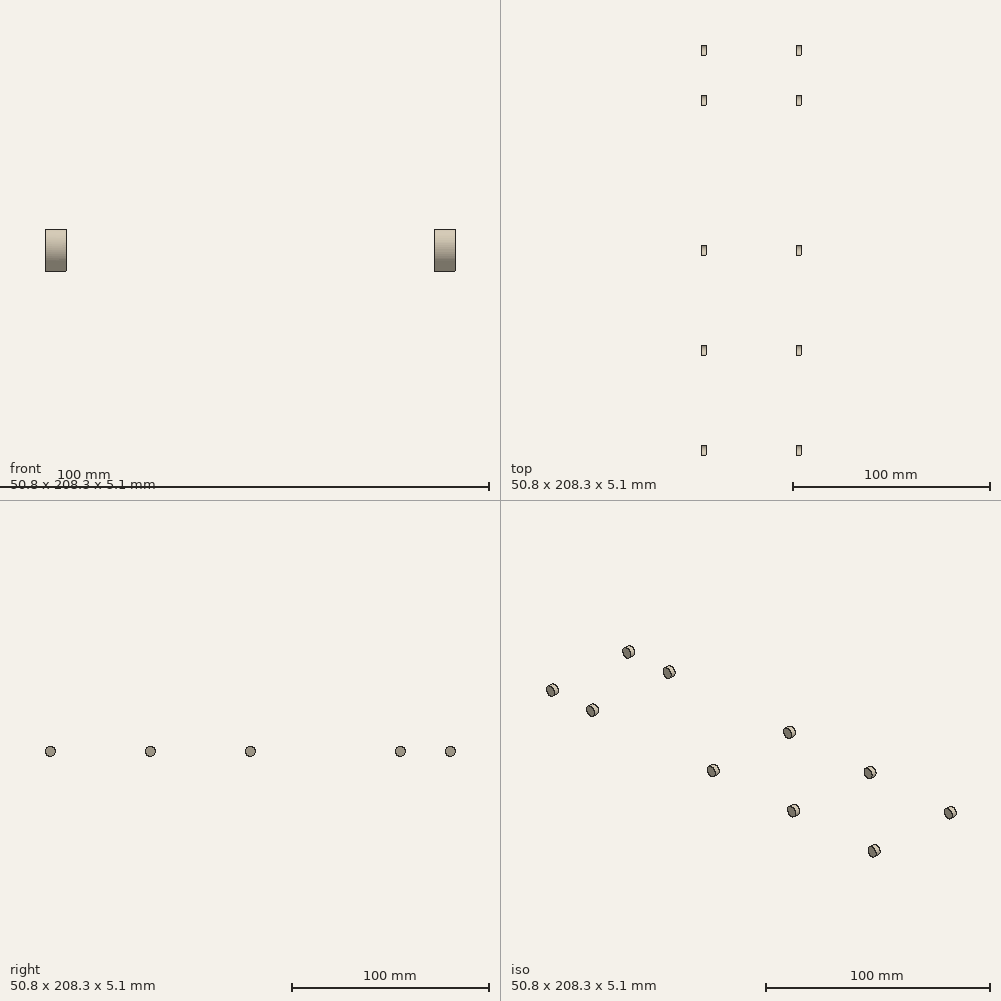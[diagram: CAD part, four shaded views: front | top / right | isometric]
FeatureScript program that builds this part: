
annotation { "Feature Type Name" : "Feature", "Feature Type Description" : "" }
export const myFeature = defineFeature(function(context is Context, id is Id, definition is map)
    precondition{}
    {
        {
            var Q0;
            Q0=qCreatedBy(makeId("Front.planeOp"),FACE);
            var sketch = newSketch(context, id + "F0", { "sketchPlane" : qUnion([Q0])});
            skLineSegment(sketch, "E0.bottom", {"start": v(0, 0) * mm, "end": v(50.8, 0) * mm});
            skLineSegment(sketch, "E0.top", {"start": v(0, 25.4) * mm, "end": v(50.8, 25.4) * mm});
            skLineSegment(sketch, "E0.left", {"start": v(0, 0) * mm, "end": v(0, 25.4) * mm});
            skLineSegment(sketch, "E0.right", {"start": v(50.8, 0) * mm, "end": v(50.8, 25.4) * mm});
            skLineSegment(sketch, "E1.bottom", {"start": v(2.54, 22.86) * mm, "end": v(48.26, 22.86) * mm});
            skLineSegment(sketch, "E1.top", {"start": v(2.54, 2.54) * mm, "end": v(48.26, 2.54) * mm});
            skLineSegment(sketch, "E1.left", {"start": v(2.54, 22.86) * mm, "end": v(2.54, 2.54) * mm});
            skLineSegment(sketch, "E1.right", {"start": v(48.26, 22.86) * mm, "end": v(48.26, 2.54) * mm});
            skSolve(sketch);
        }
        {
            var Q0;
            Q0=makeQuery(id+"F0.imprint","IMPRINT",FACE,{"disambiguationData":[TD([[makeQuery(id+"F0.imprint","IMPRINT",EDGE,{"derivedFrom":sQuery(id+"F0.wireOp",EDGE,"E0.bottom")}),1.0]])]});
            extrude(context, id + "F1", {"entities" : qUnion([Q0]), "depth" : 254 * mm, "offsetDistance" : 25.4 * mm});
        }
        {
            var Q0;
            Q0=makeQuery(id+"F1.opExtrude","SWEPT_FACE",FACE,{"disambiguationData":[OSD([sQuery(id+"F0.wireOp",EDGE,"E0.right")])]});
            var sketch = newSketch(context, id + "F2", { "sketchPlane" : qUnion([Q0])});
            skLineSegment(sketch, "E2", {"start": v(0, 12.7) * mm, "end": v(-254, 12.7) * mm});
            skCircle(sketch, "E3", {"center": v(-12.7, 12.7) * mm, "radius": 2.55 * mm});
            skCircle(sketch, "E4", {"center": v(-38.1, 12.7) * mm, "radius": 2.55 * mm});
            skCircle(sketch, "E5", {"center": v(-63.5, 12.7) * mm, "radius": 2.55 * mm});
            skCircle(sketch, "E6", {"center": v(-88.9, 12.7) * mm, "radius": 2.55 * mm});
            skCircle(sketch, "E7", {"center": v(-241.3, 12.7) * mm, "radius": 2.55 * mm});
            skCircle(sketch, "E8", {"center": v(-215.9, 12.7) * mm, "radius": 2.55 * mm});
            skCircle(sketch, "E9", {"center": v(-190.5, 12.7) * mm, "radius": 2.55 * mm});
            skCircle(sketch, "E10", {"center": v(-165.1, 12.7) * mm, "radius": 2.55 * mm});
            skCircle(sketch, "E11.1.0.0", {"center": v(-139.7, 12.7) * mm, "radius": 2.55 * mm});
            skCircle(sketch, "E11.2.0.0", {"center": v(-114.3, 12.7) * mm, "radius": 2.55 * mm});
            skLineSegment(sketch, "E11.direction1", {"start": v(-165.1, 12.7) * mm, "end": v(-139.7, 12.7) * mm, "construction": true});
            skSolve(sketch);
        }
        {
            var Q0;
            {var subQ0=sQuery(id+"F2.wireOp",EDGE,"E6");var subQ1=sQuery(id+"F2.wireOp",EDGE,"E2");var subQ2=makeQuery(id+"F2.imprint","INTERSECT",VERTEX,{"disambiguationData":[OD(0.0)],"derivedFrom":[subQ1,subQ0]});Q0=makeQuery(id+"F2.imprint","IMPRINT",FACE,{"disambiguationData":[TD([[makeQuery(id+"F2.imprint","IMPRINT",EDGE,{"disambiguationData":[TD([[subQ2,-1.0]])],"derivedFrom":subQ1}),1.0]])]});}
            var Q1;
            {var subQ0=sQuery(id+"F2.wireOp",EDGE,"E5");var subQ1=sQuery(id+"F2.wireOp",EDGE,"E2");var subQ2=makeQuery(id+"F2.imprint","INTERSECT",VERTEX,{"disambiguationData":[OD(0.0)],"derivedFrom":[subQ1,subQ0]});Q1=makeQuery(id+"F2.imprint","IMPRINT",FACE,{"disambiguationData":[TD([[makeQuery(id+"F2.imprint","IMPRINT",EDGE,{"disambiguationData":[TD([[subQ2,-1.0]])],"derivedFrom":subQ1}),1.0]])]});}
            var Q2;
            {var subQ0=sQuery(id+"F2.wireOp",EDGE,"E5");var subQ1=sQuery(id+"F2.wireOp",EDGE,"E2");var subQ2=makeQuery(id+"F2.imprint","INTERSECT",VERTEX,{"disambiguationData":[OD(0.0)],"derivedFrom":[subQ1,subQ0]});Q2=makeQuery(id+"F2.imprint","IMPRINT",FACE,{"disambiguationData":[TD([[makeQuery(id+"F2.imprint","IMPRINT",EDGE,{"disambiguationData":[TD([[subQ2,-1.0]])],"derivedFrom":subQ1}),-1.0]])]});}
            var Q3;
            {var subQ0=sQuery(id+"F2.wireOp",EDGE,"E4");var subQ1=sQuery(id+"F2.wireOp",EDGE,"E2");var subQ2=makeQuery(id+"F2.imprint","INTERSECT",VERTEX,{"disambiguationData":[OD(0.0)],"derivedFrom":[subQ1,subQ0]});Q3=makeQuery(id+"F2.imprint","IMPRINT",FACE,{"disambiguationData":[TD([[makeQuery(id+"F2.imprint","IMPRINT",EDGE,{"disambiguationData":[TD([[subQ2,-1.0]])],"derivedFrom":subQ1}),1.0]])]});}
            var Q4;
            {var subQ0=sQuery(id+"F2.wireOp",EDGE,"E4");var subQ1=sQuery(id+"F2.wireOp",EDGE,"E2");var subQ2=makeQuery(id+"F2.imprint","INTERSECT",VERTEX,{"disambiguationData":[OD(0.0)],"derivedFrom":[subQ1,subQ0]});Q4=makeQuery(id+"F2.imprint","IMPRINT",FACE,{"disambiguationData":[TD([[makeQuery(id+"F2.imprint","IMPRINT",EDGE,{"disambiguationData":[TD([[subQ2,-1.0]])],"derivedFrom":subQ1}),-1.0]])]});}
            var Q5;
            {var subQ0=sQuery(id+"F2.wireOp",EDGE,"E3");var subQ1=sQuery(id+"F2.wireOp",EDGE,"E2");var subQ2=makeQuery(id+"F2.imprint","INTERSECT",VERTEX,{"disambiguationData":[OD(0.0)],"derivedFrom":[subQ1,subQ0]});Q5=makeQuery(id+"F2.imprint","IMPRINT",FACE,{"disambiguationData":[TD([[makeQuery(id+"F2.imprint","IMPRINT",EDGE,{"disambiguationData":[TD([[subQ2,-1.0]])],"derivedFrom":subQ1}),1.0]])]});}
            var Q6;
            {var subQ0=sQuery(id+"F2.wireOp",EDGE,"E3");var subQ1=sQuery(id+"F2.wireOp",EDGE,"E2");var subQ2=makeQuery(id+"F2.imprint","INTERSECT",VERTEX,{"disambiguationData":[OD(0.0)],"derivedFrom":[subQ1,subQ0]});Q6=makeQuery(id+"F2.imprint","IMPRINT",FACE,{"disambiguationData":[TD([[makeQuery(id+"F2.imprint","IMPRINT",EDGE,{"disambiguationData":[TD([[subQ2,-1.0]])],"derivedFrom":subQ1}),-1.0]])]});}
            var Q7;
            {var subQ0=sQuery(id+"F2.wireOp",EDGE,"E6");var subQ1=sQuery(id+"F2.wireOp",EDGE,"E2");var subQ2=makeQuery(id+"F2.imprint","INTERSECT",VERTEX,{"disambiguationData":[OD(0.0)],"derivedFrom":[subQ1,subQ0]});Q7=makeQuery(id+"F2.imprint","IMPRINT",FACE,{"disambiguationData":[TD([[makeQuery(id+"F2.imprint","IMPRINT",EDGE,{"disambiguationData":[TD([[subQ2,-1.0]])],"derivedFrom":subQ1}),-1.0]])]});}
            var Q8;
            {var subQ0=sQuery(id+"F2.wireOp",EDGE,"E10");var subQ1=sQuery(id+"F2.wireOp",EDGE,"E2");var subQ2=makeQuery(id+"F2.imprint","INTERSECT",VERTEX,{"disambiguationData":[OD(0.0)],"derivedFrom":[subQ1,subQ0]});Q8=makeQuery(id+"F2.imprint","IMPRINT",FACE,{"disambiguationData":[TD([[makeQuery(id+"F2.imprint","IMPRINT",EDGE,{"disambiguationData":[TD([[subQ2,-1.0]])],"derivedFrom":subQ1}),1.0]])]});}
            var Q9;
            {var subQ0=sQuery(id+"F2.wireOp",EDGE,"E10");var subQ1=sQuery(id+"F2.wireOp",EDGE,"E2");var subQ2=makeQuery(id+"F2.imprint","INTERSECT",VERTEX,{"disambiguationData":[OD(0.0)],"derivedFrom":[subQ1,subQ0]});Q9=makeQuery(id+"F2.imprint","IMPRINT",FACE,{"disambiguationData":[TD([[makeQuery(id+"F2.imprint","IMPRINT",EDGE,{"disambiguationData":[TD([[subQ2,-1.0]])],"derivedFrom":subQ1}),-1.0]])]});}
            var Q10;
            {var subQ0=sQuery(id+"F2.wireOp",EDGE,"E9");var subQ1=sQuery(id+"F2.wireOp",EDGE,"E2");var subQ2=makeQuery(id+"F2.imprint","INTERSECT",VERTEX,{"disambiguationData":[OD(0.0)],"derivedFrom":[subQ1,subQ0]});Q10=makeQuery(id+"F2.imprint","IMPRINT",FACE,{"disambiguationData":[TD([[makeQuery(id+"F2.imprint","IMPRINT",EDGE,{"disambiguationData":[TD([[subQ2,-1.0]])],"derivedFrom":subQ1}),1.0]])]});}
            var Q11;
            {var subQ0=sQuery(id+"F2.wireOp",EDGE,"E9");var subQ1=sQuery(id+"F2.wireOp",EDGE,"E2");var subQ2=makeQuery(id+"F2.imprint","INTERSECT",VERTEX,{"disambiguationData":[OD(0.0)],"derivedFrom":[subQ1,subQ0]});Q11=makeQuery(id+"F2.imprint","IMPRINT",FACE,{"disambiguationData":[TD([[makeQuery(id+"F2.imprint","IMPRINT",EDGE,{"disambiguationData":[TD([[subQ2,-1.0]])],"derivedFrom":subQ1}),-1.0]])]});}
            var Q12;
            {var subQ0=sQuery(id+"F2.wireOp",EDGE,"E7");var subQ1=sQuery(id+"F2.wireOp",EDGE,"E2");var subQ2=makeQuery(id+"F2.imprint","INTERSECT",VERTEX,{"disambiguationData":[OD(0.0)],"derivedFrom":[subQ1,subQ0]});Q12=makeQuery(id+"F2.imprint","IMPRINT",FACE,{"disambiguationData":[TD([[makeQuery(id+"F2.imprint","IMPRINT",EDGE,{"disambiguationData":[TD([[subQ2,-1.0]])],"derivedFrom":subQ1}),1.0]])]});}
            var Q13;
            {var subQ0=sQuery(id+"F2.wireOp",EDGE,"E7");var subQ1=sQuery(id+"F2.wireOp",EDGE,"E2");var subQ2=makeQuery(id+"F2.imprint","INTERSECT",VERTEX,{"disambiguationData":[OD(0.0)],"derivedFrom":[subQ1,subQ0]});Q13=makeQuery(id+"F2.imprint","IMPRINT",FACE,{"disambiguationData":[TD([[makeQuery(id+"F2.imprint","IMPRINT",EDGE,{"disambiguationData":[TD([[subQ2,-1.0]])],"derivedFrom":subQ1}),-1.0]])]});}
            var Q14;
            {var subQ0=sQuery(id+"F2.wireOp",EDGE,"E8");var subQ1=sQuery(id+"F2.wireOp",EDGE,"E2");var subQ2=makeQuery(id+"F2.imprint","INTERSECT",VERTEX,{"disambiguationData":[OD(0.0)],"derivedFrom":[subQ1,subQ0]});Q14=makeQuery(id+"F2.imprint","IMPRINT",FACE,{"disambiguationData":[TD([[makeQuery(id+"F2.imprint","IMPRINT",EDGE,{"disambiguationData":[TD([[subQ2,-1.0]])],"derivedFrom":subQ1}),1.0]])]});}
            var Q15;
            {var subQ0=sQuery(id+"F2.wireOp",EDGE,"E8");var subQ1=sQuery(id+"F2.wireOp",EDGE,"E2");var subQ2=makeQuery(id+"F2.imprint","INTERSECT",VERTEX,{"disambiguationData":[OD(0.0)],"derivedFrom":[subQ1,subQ0]});Q15=makeQuery(id+"F2.imprint","IMPRINT",FACE,{"disambiguationData":[TD([[makeQuery(id+"F2.imprint","IMPRINT",EDGE,{"disambiguationData":[TD([[subQ2,-1.0]])],"derivedFrom":subQ1}),-1.0]])]});}
            var Q16;
            {var subQ0=sQuery(id+"F2.wireOp",EDGE,"E11.1.0.0");var subQ1=sQuery(id+"F2.wireOp",EDGE,"E2");var subQ2=makeQuery(id+"F2.imprint","INTERSECT",VERTEX,{"disambiguationData":[OD(0.0)],"derivedFrom":[subQ1,subQ0]});Q16=makeQuery(id+"F2.imprint","IMPRINT",FACE,{"disambiguationData":[TD([[makeQuery(id+"F2.imprint","IMPRINT",EDGE,{"disambiguationData":[TD([[subQ2,-1.0]])],"derivedFrom":subQ1}),-1.0]])]});}
            var Q17;
            {var subQ0=sQuery(id+"F2.wireOp",EDGE,"E11.1.0.0");var subQ1=sQuery(id+"F2.wireOp",EDGE,"E2");var subQ2=makeQuery(id+"F2.imprint","INTERSECT",VERTEX,{"disambiguationData":[OD(0.0)],"derivedFrom":[subQ1,subQ0]});Q17=makeQuery(id+"F2.imprint","IMPRINT",FACE,{"disambiguationData":[TD([[makeQuery(id+"F2.imprint","IMPRINT",EDGE,{"disambiguationData":[TD([[subQ2,-1.0]])],"derivedFrom":subQ1}),1.0]])]});}
            var Q18;
            {var subQ0=sQuery(id+"F2.wireOp",EDGE,"E11.2.0.0");var subQ1=sQuery(id+"F2.wireOp",EDGE,"E2");var subQ2=makeQuery(id+"F2.imprint","INTERSECT",VERTEX,{"disambiguationData":[OD(0.0)],"derivedFrom":[subQ1,subQ0]});Q18=makeQuery(id+"F2.imprint","IMPRINT",FACE,{"disambiguationData":[TD([[makeQuery(id+"F2.imprint","IMPRINT",EDGE,{"disambiguationData":[TD([[subQ2,-1.0]])],"derivedFrom":subQ1}),-1.0]])]});}
            var Q19;
            {var subQ0=sQuery(id+"F2.wireOp",EDGE,"E11.2.0.0");var subQ1=sQuery(id+"F2.wireOp",EDGE,"E2");var subQ2=makeQuery(id+"F2.imprint","INTERSECT",VERTEX,{"disambiguationData":[OD(0.0)],"derivedFrom":[subQ1,subQ0]});Q19=makeQuery(id+"F2.imprint","IMPRINT",FACE,{"disambiguationData":[TD([[makeQuery(id+"F2.imprint","IMPRINT",EDGE,{"disambiguationData":[TD([[subQ2,-1.0]])],"derivedFrom":subQ1}),1.0]])]});}
            extrude(context, id + "F3", {"entities" : qUnion([Q0, Q1, Q2, Q3, Q4, Q5, Q6, Q7, Q8, Q9, Q10, Q11, Q12, Q13, Q14, Q15, Q16, Q17, Q18, Q19]), "operationType" : NewBodyOperationType.REMOVE, "oppositeDirection" : true, "depth" : 127 * mm, "offsetDistance" : 25.4 * mm});
        }
    });
